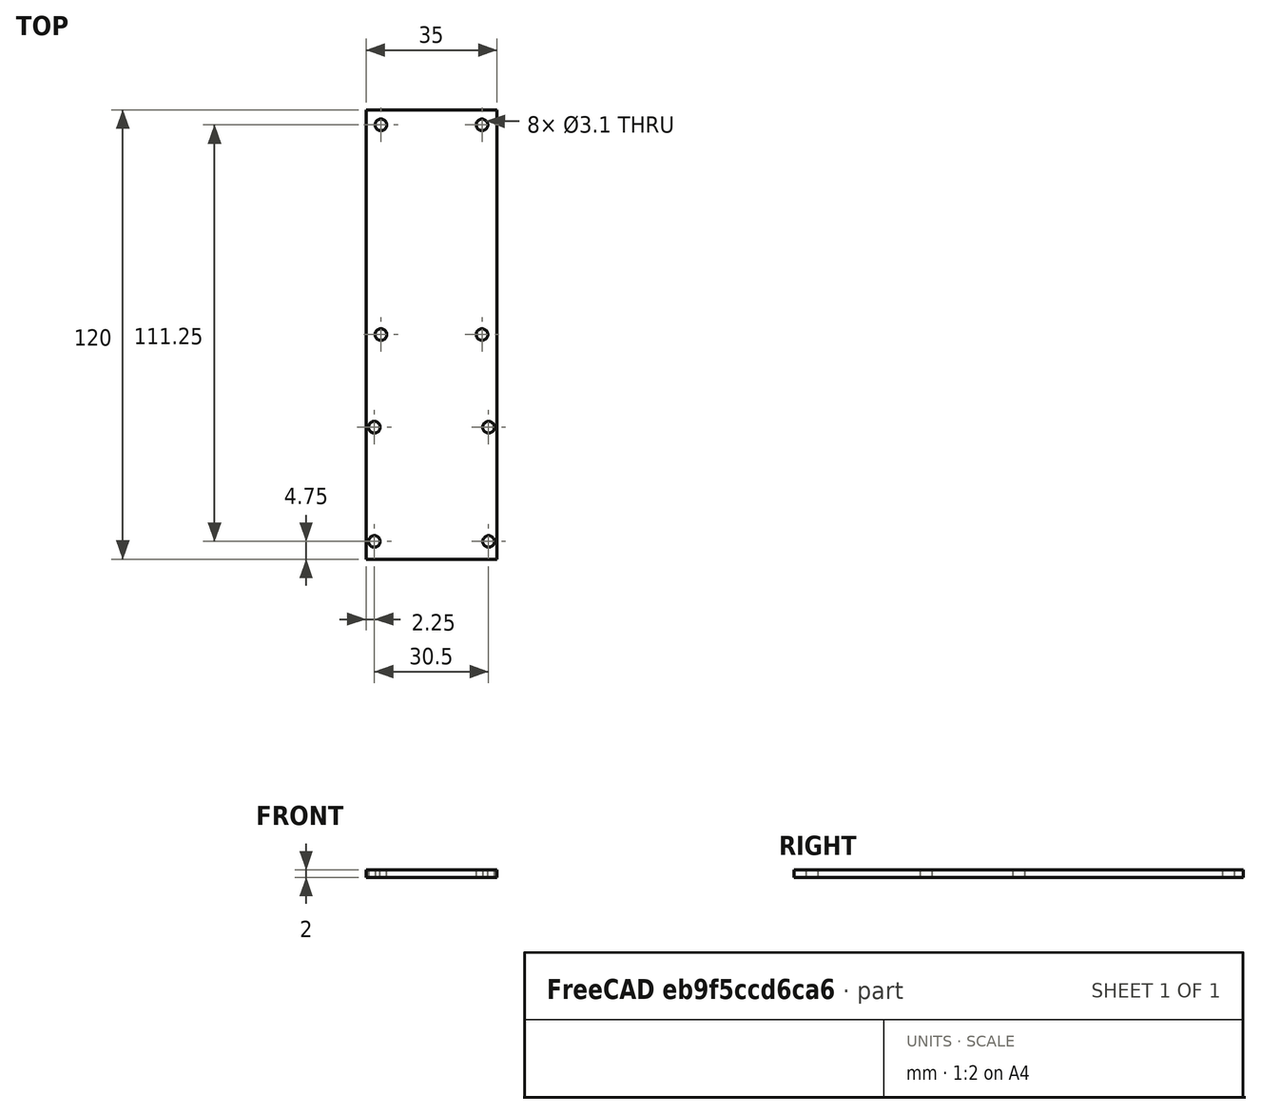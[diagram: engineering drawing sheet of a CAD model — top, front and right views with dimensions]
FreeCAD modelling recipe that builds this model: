
FCSTD DOCUMENT  (FreeCAD 0.20R29410 (Git))
Label: middle_plate
License: All rights reserved
LicenseURL: http://en.wikipedia.org/wiki/All_rights_reserved
objects: PartDesign::CoordinateSystem×5, Sketcher::SketchObject×1, PartDesign::Pad×1, PartDesign::Body×1
note: 9 computed .brp shape members not serialized (recipe doc carries the construction recipe); baked Part::Feature solids carry a one-line shape summary decoded from their .brp

FEATURE [Sketcher::SketchObject] Sketch
  FullyConstrained = true
  MapMode = 5
  Support = -> [XY_Plane]
  sketch-geometry (12):
    g0: LineSegment StartX=-17.5 StartY=100 StartZ=0 EndX=17.5 EndY=100 EndZ=0
    g1: LineSegment StartX=17.5 StartY=100 StartZ=0 EndX=17.5 EndY=-20 EndZ=0
    g2: LineSegment StartX=17.5 StartY=-20 StartZ=0 EndX=-17.5 EndY=-20 EndZ=0
    g3: LineSegment StartX=-17.5 StartY=-20 StartZ=0 EndX=-17.5 EndY=100 EndZ=0
    g4: Circle CenterX=-15.25 CenterY=15.25 CenterZ=0 NormalX=0 NormalY=0 NormalZ=1 AngleXU=0 Radius=1.55
    g5: Circle CenterX=15.25 CenterY=15.25 CenterZ=0 NormalX=0 NormalY=0 NormalZ=1 AngleXU=0 Radius=1.55
    g6: Circle CenterX=-15.25 CenterY=-15.25 CenterZ=0 NormalX=0 NormalY=0 NormalZ=1 AngleXU=0 Radius=1.55
    g7: Circle CenterX=15.25 CenterY=-15.25 CenterZ=0 NormalX=0 NormalY=0 NormalZ=1 AngleXU=0 Radius=1.55
    g8: Circle CenterX=-13.5 CenterY=96 CenterZ=0 NormalX=0 NormalY=0 NormalZ=1 AngleXU=0 Radius=1.55
    g9: Circle CenterX=13.5 CenterY=96 CenterZ=0 NormalX=0 NormalY=0 NormalZ=1 AngleXU=0 Radius=1.55
    g10: Circle CenterX=-13.5 CenterY=40 CenterZ=0 NormalX=0 NormalY=0 NormalZ=1 AngleXU=0 Radius=1.55
    g11: Circle CenterX=13.5 CenterY=40 CenterZ=0 NormalX=0 NormalY=0 NormalZ=1 AngleXU=0 Radius=1.55
  constraints (30):
    c: Coincident(g0,g1)
    c: Coincident(g1,g2)
    c: Coincident(g2,g3)
    c: Coincident(g3,g0)
    c: Horizontal(g0)
    c: Vertical(g1)
    c: Vertical(g3)
    c: DistanceX(g2,g2) = 35
    c: Equal(g7,g6)
    c: Equal(g6,g4)
    c: Equal(g4,g5)
    c: Symmetric(g6,g7,g-2)
    c: Symmetric(g4,g6,g-1)
    c: Symmetric(g5,g7,g-1)
    c: Diameter(g7) = 3.1
    c: DistanceX(g6,g7) = 30.5
    c: DistanceY(g7,g5) = 30.5
    c: Symmetric(g2,g1,g-2)
    c: DistanceY(g1,g-1) = 20
    c: DistanceY(g3,g3) = 120
    c: Symmetric(g8,g9,g-2)
    c: Diameter(g9) = 3.1
    c: Equal(g9,g8)
    c: DistanceX(g9,g0) = 4
    c: DistanceY(g9,g0) = 4
    c: Equal(g11,g10)
    c: Symmetric(g10,g11,g-2)
    c: Diameter(g11) = 3.1
    c: DistanceX(g11,g0) = 4
    c: DistanceY(g11,g0) = 60
FEATURE [PartDesign::Pad] Pad
  Direction = (0,0,1)
  Length = 2
  Length2 = 10
  Profile = -> Sketch
  ReferenceAxis = -> Sketch [N_Axis]
  Type = 0
FEATURE [PartDesign::CoordinateSystem] LCS_1
  AttacherType = Attacher::AttachEngine3D
  MapMode = 11
  Placement = pos=(15.25,15.25,0) rot=(0,0,1;1.5708rad)
  Support = -> [Pad]
FEATURE [PartDesign::CoordinateSystem] LCS_2
  AttacherType = Attacher::AttachEngine3D
  MapMode = 11
  Placement = pos=(-13.5,96,2) rot=(0,0,1;1.5708rad)
  Support = -> [Pad]
FEATURE [PartDesign::CoordinateSystem] LCS_3
  AttacherType = Attacher::AttachEngine3D
  MapMode = 11
  Placement = pos=(13.5,96,2) rot=(0,0,1;1.5708rad)
  Support = -> [Pad]
FEATURE [PartDesign::CoordinateSystem] LCS_4
  AttacherType = Attacher::AttachEngine3D
  MapMode = 11
  Placement = pos=(-13.5,40,2) rot=(0,0,1;1.5708rad)
  Support = -> [Pad]
FEATURE [PartDesign::CoordinateSystem] LCS_5
  AttacherType = Attacher::AttachEngine3D
  MapMode = 11
  Placement = pos=(13.5,40,2) rot=(0,0,1;1.5708rad)
  Support = -> [Pad]
FEATURE [PartDesign::Body] Body
  Group = -> [Sketch,Pad,LCS_1,LCS_2,LCS_3,LCS_4,LCS_5]
  Origin = -> Origin
  Tip = -> Pad
